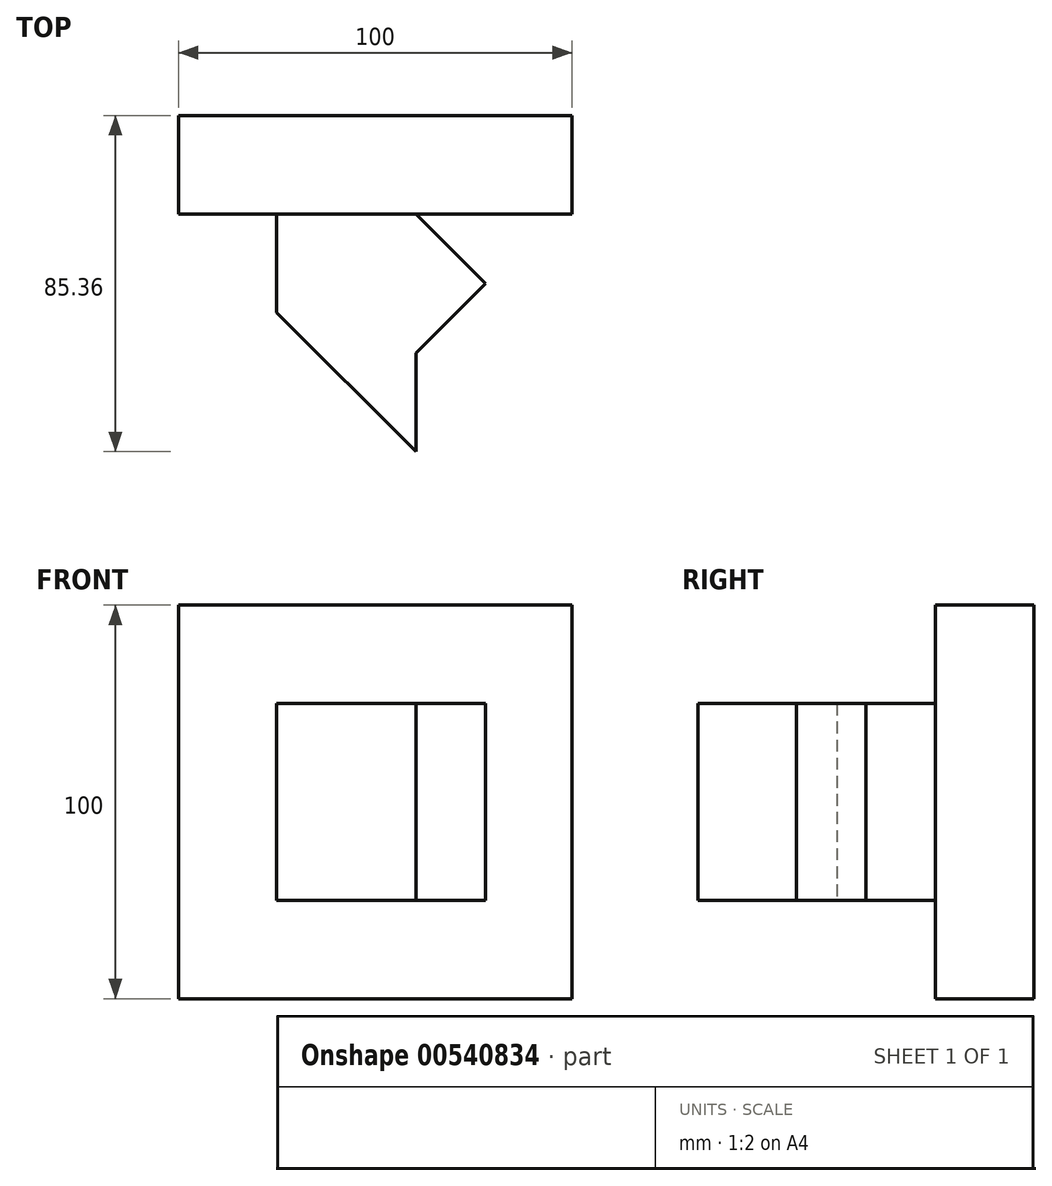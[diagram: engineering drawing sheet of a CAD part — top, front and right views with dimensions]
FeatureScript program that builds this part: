
annotation { "Feature Type Name" : "Feature", "Feature Type Description" : "" }
export const myFeature = defineFeature(function(context is Context, id is Id, definition is map)
    precondition{}
    {
        {
            var Q0;
            Q0=qCreatedBy(makeId("Front.planeOp"),FACE);
            var sketch = newSketch(context, id + "F0", { "sketchPlane" : qUnion([Q0])});
            skLineSegment(sketch, "E0.bottom", {"start": v(-50, 50) * mm, "end": v(50, 50) * mm});
            skLineSegment(sketch, "E0.top", {"start": v(-50, -50) * mm, "end": v(50, -50) * mm});
            skLineSegment(sketch, "E0.left", {"start": v(-50, 50) * mm, "end": v(-50, -50) * mm});
            skLineSegment(sketch, "E0.right", {"start": v(50, 50) * mm, "end": v(50, -50) * mm});
            skPoint(sketch, "E0.middle", {"position": v(0, 0) * mm});
            skSolve(sketch);
        }
        {
            var Q0;
            Q0=qCreatedBy(makeId("Front.planeOp"),FACE);
            var sketch = newSketch(context, id + "F1", { "sketchPlane" : qUnion([Q0])});
            skLineSegment(sketch, "E1.bottom", {"start": v(-25, 25) * mm, "end": v(25, 25) * mm});
            skLineSegment(sketch, "E1.top", {"start": v(-25, -25) * mm, "end": v(25, -25) * mm});
            skLineSegment(sketch, "E1.left", {"start": v(-25, 25) * mm, "end": v(-25, -25) * mm});
            skLineSegment(sketch, "E1.right", {"start": v(25, 25) * mm, "end": v(25, -25) * mm});
            skPoint(sketch, "E1.middle", {"position": v(0, 0) * mm});
            skSolve(sketch);
        }
        {
            var Q0;
            Q0 = qSketchRegion(id + "F1", true);
            extrude(context, id + "F2", {"entities" : qUnion([Q0]), "depth" : 25 * mm, "offsetDistance" : 25 * mm});
        }
        {
            var Q0;
            Q0=makeQuery(id+"F2.opExtrude","SWEPT_BODY",BODY,{"disambiguationData":[OSD([sQuery(id+"F1.wireOp",EDGE,"E1.bottom"),sQuery(id+"F1.wireOp",EDGE,"E1.top"),sQuery(id+"F1.wireOp",EDGE,"E1.left"),sQuery(id+"F1.wireOp",EDGE,"E1.right")])]});
            var Q1;
            Q1=makeQuery(id+"F2.opExtrude","CAP_EDGE",EDGE,{"disambiguationData":[OSD([sQuery(id+"F1.wireOp",EDGE,"E1.left")])],"isStart":false});
            transform(context, id + "F3", {"entities" : qUnion([Q0]), "transformType" : TransformType.ROTATION, "transformAxis" : qUnion([Q1]), "angle" : 45 * degree, "makeCopy" : false});
        }
        {
            var Q0;
            Q0=makeQuery(id+"F0.imprint","IMPRINT",FACE,{"disambiguationData":[TD([[makeQuery(id+"F0.imprint","IMPRINT",EDGE,{"derivedFrom":sQuery(id+"F0.wireOp",EDGE,"E0.bottom")}),-1.0]])]});
            var Q1;
            Q1=makeQuery(id+"F2.opExtrude","CAP_FACE",FACE,{"disambiguationData":[OSD([sQuery(id+"F1.wireOp",EDGE,"E1.bottom"),sQuery(id+"F1.wireOp",EDGE,"E1.top"),sQuery(id+"F1.wireOp",EDGE,"E1.left"),sQuery(id+"F1.wireOp",EDGE,"E1.right")])],"isStart":false});
            extrude(context, id + "F4", {"entities" : qUnion([Q0, Q1]), "operationType" : NewBodyOperationType.ADD, "depth" : 25 * mm, "offsetDistance" : 25 * mm});
        }
    });
